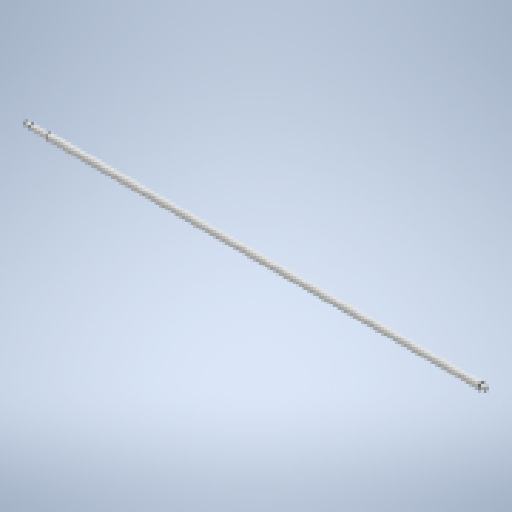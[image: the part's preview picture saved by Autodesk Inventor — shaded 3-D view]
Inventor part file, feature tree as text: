
AUTODESK INVENTOR PART (.ipt)
format: ipt  version: 2023 (Build 270158000, 158)  size: 249,856 bytes
history: native  units: mm
features: revolve x1, sketch x1
ambient origin geometry x8: Origin, YZ Plane, XZ Plane, XY Plane, X Axis, Y Axis, Z Axis, Center Point
bodies: Solid1 (feature_tree)
feature tree (2):
  revolve  "Revolution1"  [1 undecoded]
  sketch  "Sketch1"  dims[d0=5.0mm d1=6.0mm d2=8.0mm d3=5.0mm d4=11.0mm d6=39.0mm d8=15.0mm d9=1100.0mm d10=90.0deg]
note: 1 required parameter value undecoded (feature->parameter linkage not recoverable at this tier; creation-order binding heuristic only, values carry confidence <= 0.55)
